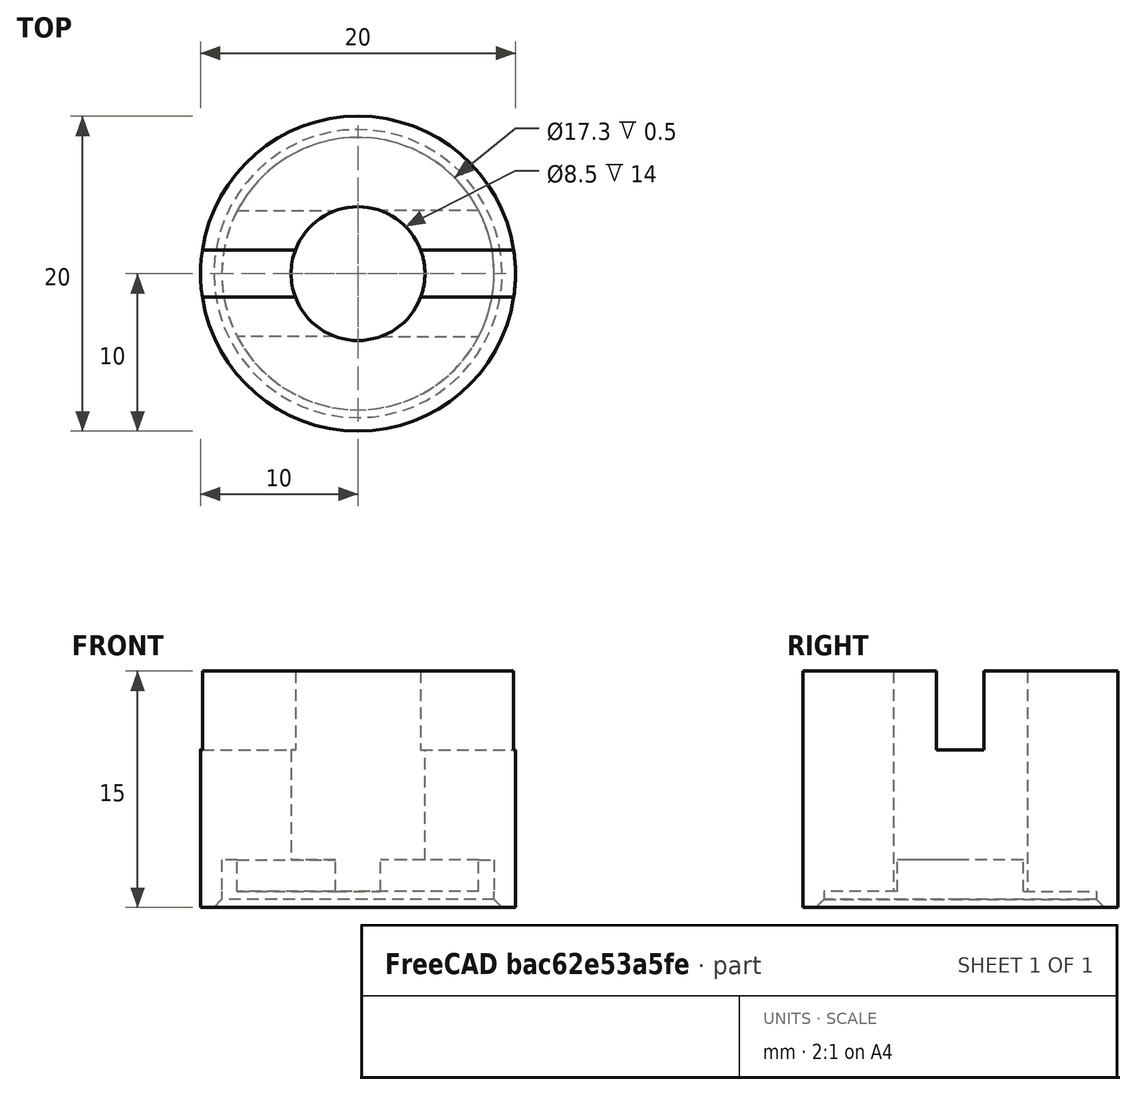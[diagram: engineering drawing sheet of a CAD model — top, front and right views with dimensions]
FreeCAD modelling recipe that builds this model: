
FCSTD DOCUMENT  (FreeCAD 0.19R)
Label: support_led_Tal
License: All rights reserved
LicenseURL: http://en.wikipedia.org/wiki/All_rights_reserved
objects: Sketcher::SketchObject×4, PartDesign::Pocket×3, App::Part×1, PartDesign::Pad×1, PartDesign::Mirrored×1, PartDesign::Chamfer×1, PartDesign::Body×1, Mesh::Feature×1, App::DocumentObjectGroup×1
note: 16 computed .brp shape members not serialized (recipe doc carries the construction recipe); baked Part::Feature solids carry a one-line shape summary decoded from their .brp

FEATURE [App::Part] Part
  Origin = -> Origin
FEATURE [Sketcher::SketchObject] Sketch
  FullyConstrained = false
  MapMode = 5
  Support = -> [XY_Plane001]
  sketch-geometry (2):
    g0: Circle CenterX=0 CenterY=0 CenterZ=0 NormalX=0 NormalY=0 NormalZ=1 AngleXU=0 Radius=10
    g1: Circle CenterX=0 CenterY=0 CenterZ=0 NormalX=0 NormalY=0 NormalZ=1 AngleXU=0 Radius=4.25
  constraints (4):
    c: Coincident(g0,g-1)
    c: Radius(g0) = 10
    c: Coincident(g1,g0)
    c: Radius(g1) = 4.25
FEATURE [PartDesign::Pad] Pad
  AllowMultiFace = false
  Direction = (1,1,1)
  Length = 15
  Length2 = 100
  Profile = -> Sketch
  Type = 0
FEATURE [Sketcher::SketchObject] Sketch001
  ExternalGeometry = -> [Pad]
  FullyConstrained = true
  MapMode = 5
  Placement = pos=(0,0,15) rot=(0,0,1;0rad)
  Support = -> [Pad]
  sketch-geometry (8):
    g0: LineSegment StartX=-9.88686 StartY=1.5 StartZ=0 EndX=-3.97649 EndY=1.5 EndZ=0
    g1: LineSegment StartX=3.97649 StartY=1.5 StartZ=0 EndX=9.88686 EndY=1.5 EndZ=0
    g2: LineSegment StartX=-9.88686 StartY=-1.5 StartZ=0 EndX=-3.97649 EndY=-1.5 EndZ=0
    g3: LineSegment StartX=3.97649 StartY=-1.5 StartZ=0 EndX=9.88686 EndY=-1.5 EndZ=0
    g4: ArcOfCircle CenterX=0 CenterY=0 CenterZ=0 NormalX=0 NormalY=0 NormalZ=1 AngleXU=0 Radius=10 StartAngle=2.99102 EndAngle=3.29216
    g5: ArcOfCircle CenterX=0 CenterY=0 CenterZ=0 NormalX=0 NormalY=0 NormalZ=1 AngleXU=0 Radius=4.25 StartAngle=2.78088 EndAngle=3.50231
    g6: ArcOfCircle CenterX=0 CenterY=0 CenterZ=0 NormalX=0 NormalY=0 NormalZ=1 AngleXU=0 Radius=10 StartAngle=6.13262 EndAngle=6.43375
    g7: ArcOfCircle CenterX=0 CenterY=0 CenterZ=0 NormalX=0 NormalY=0 NormalZ=1 AngleXU=0 Radius=4.25 StartAngle=5.92247 EndAngle=6.6439
  constraints (27):
    c: PointOnObject(g0,g-4)
    c: PointOnObject(g0,g-3)
    c: Horizontal(g0)
    c: PointOnObject(g1,g-4)
    c: Horizontal(g2)
    c: PointOnObject(g3,g-3)
    c: PointOnObject(g3,g-4)
    c: Horizontal(g3)
    c: Horizontal(g1)
    c: DistanceY(g-1,g0) = 1.5
    c: Horizontal(g0,g1)
    c: PointOnObject(g1,g-3)
    c: Horizontal(g2,g3)
    c: Coincident(g4,g0)
    c: Coincident(g4,g2)
    c: Coincident(g5,g4)
    c: Coincident(g5,g0)
    c: Coincident(g5,g2)
    c: DistanceY(g2,g4) = 1.5
    c: Coincident(g6,g3)
    c: Coincident(g6,g1)
    c: Coincident(g4,g6)
    c: Coincident(g4,g-4)
    c: Coincident(g4,g-3)
    c: Coincident(g7,g4)
    c: Coincident(g7,g3)
    c: Coincident(g7,g1)
FEATURE [PartDesign::Pocket] Pocket
  AllowMultiFace = false
  BaseFeature = -> Pad
  Length = 5
  Length2 = 100
  Profile = -> Sketch001
  Type = 0
FEATURE [Sketcher::SketchObject] Sketch002
  FullyConstrained = true
  MapMode = 5
  Placement = pos=(0,0,0) rot=(1,0,0;3.14159rad)
  Support = -> [Pocket]
  sketch-geometry (1):
    g0: Circle CenterX=0 CenterY=0 CenterZ=0 NormalX=0 NormalY=0 NormalZ=1 AngleXU=0 Radius=8.65
  constraints (2):
    c: Coincident(g0,g-1)
    c: Diameter(g0) = 17.3
FEATURE [PartDesign::Pocket] Pocket001
  AllowMultiFace = false
  BaseFeature = -> Pocket
  Length = 1
  Length2 = 100
  Profile = -> Sketch002
  Type = 0
FEATURE [Sketcher::SketchObject] Sketch003
  ExternalGeometry = -> [Pocket001]
  FullyConstrained = true
  MapMode = 5
  Placement = pos=(0,0,1) rot=(1,0,0;3.14159rad)
  Support = -> [Pocket001]
  sketch-geometry (4):
    g0: LineSegment StartX=1.43614 StartY=4 StartZ=0 EndX=7.66958 EndY=4 EndZ=0
    g1: ArcOfCircle CenterX=0 CenterY=0 CenterZ=0 NormalX=0 NormalY=0 NormalZ=1 AngleXU=0 Radius=8.65 StartAngle=5.80245 EndAngle=6.76392
    g2: LineSegment StartX=7.66958 StartY=-4 StartZ=0 EndX=1.43614 EndY=-4 EndZ=0
    g3: ArcOfCircle CenterX=0 CenterY=0 CenterZ=0 NormalX=0 NormalY=0 NormalZ=1 AngleXU=0 Radius=4.25 StartAngle=5.05709 EndAngle=7.50928
  constraints (12):
    c: PointOnObject(g0,g-3)
    c: PointOnObject(g0,g-4)
    c: Horizontal(g0)
    c: Horizontal(g2)
    c: Coincident(g1,g-1)
    c: Coincident(g1,g0)
    c: Coincident(g1,g2)
    c: Vertical(g2,g0)
    c: Coincident(g3,g1)
    c: Coincident(g3,g2)
    c: Coincident(g3,g0)
    c: DistanceY(g2,g1) = 4
FEATURE [PartDesign::Pocket] Pocket002
  AllowMultiFace = false
  BaseFeature = -> Pocket001
  Length = 2
  Length2 = 100
  Profile = -> Sketch003
  Type = 0
FEATURE [PartDesign::Mirrored] Mirrored
  BaseFeature = -> Pocket002
  MirrorPlane = -> YZ_Plane001
  Originals = -> [Pocket002]
FEATURE [PartDesign::Chamfer] Chamfer
  Angle = 45
  Base = -> Mirrored [Edge12]
  BaseFeature = -> Mirrored
  ChamferType = 0
  FlipDirection = false
  Size = 0.5
  Size2 = 1
  SupportTransform = false
FEATURE [PartDesign::Body] Body
  Group = -> [Sketch,Pad,Sketch001,Pocket,Sketch002,Pocket001,Sketch003,Pocket002,Mirrored,Chamfer]
  Origin = -> Origin001
  Tip = -> Chamfer
FEATURE [Mesh::Feature] Mesh  label="Body (Meshed)"
FEATURE [App::DocumentObjectGroup] Group  label="stl"
  Group = -> [Mesh]
